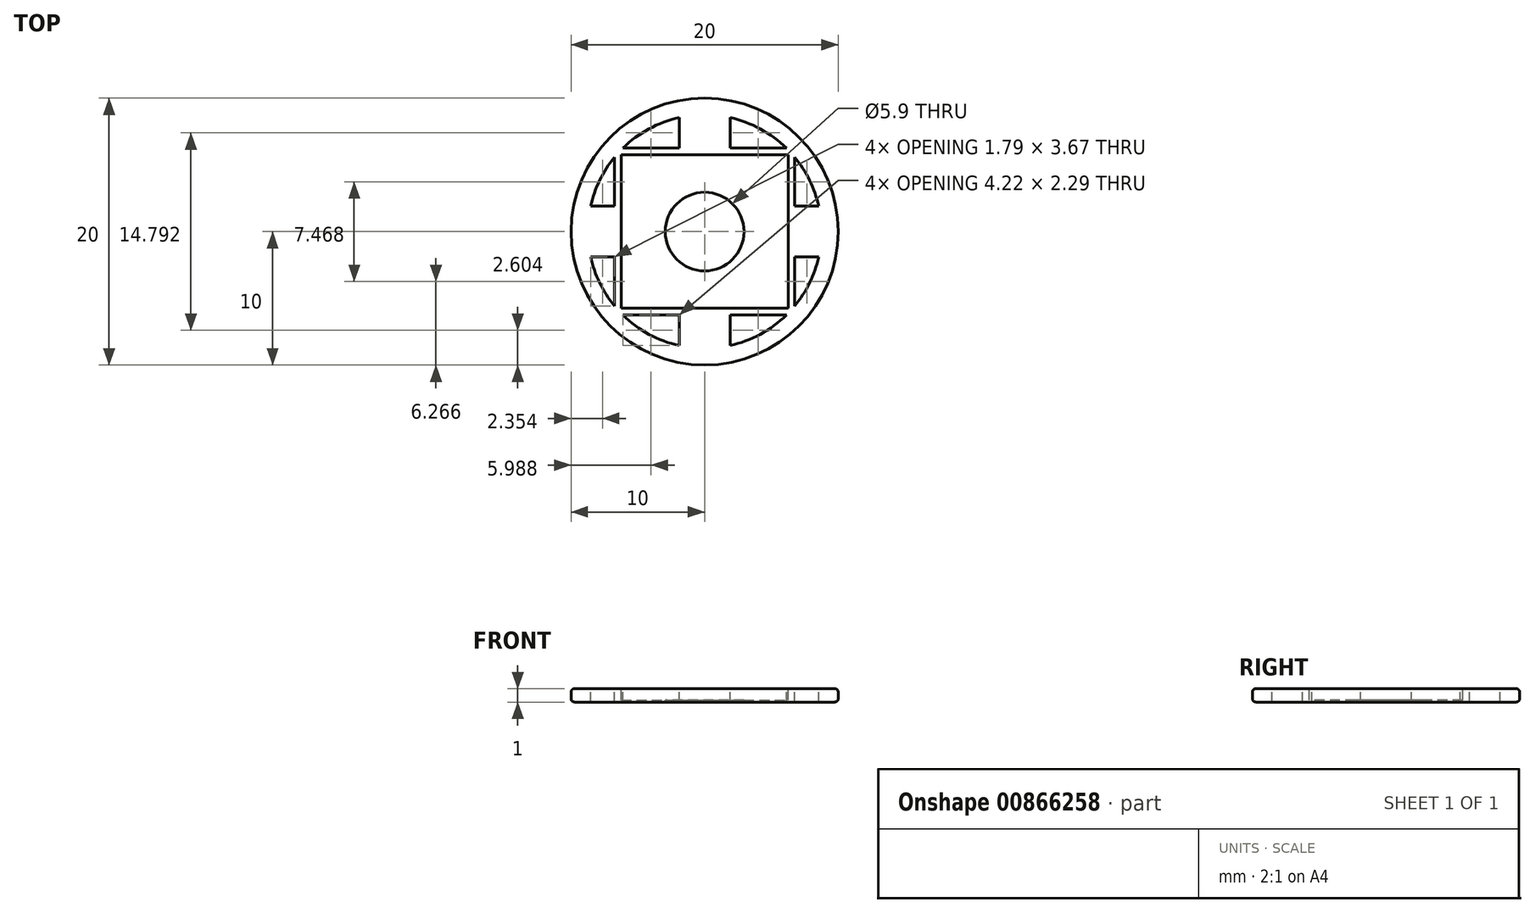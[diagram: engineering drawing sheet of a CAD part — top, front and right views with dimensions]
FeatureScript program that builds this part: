
annotation { "Feature Type Name" : "Feature", "Feature Type Description" : "" }
export const myFeature = defineFeature(function(context is Context, id is Id, definition is map)
    precondition{}
    {
        {
            var Q0;
            Q0=qCreatedBy(makeId("Top.planeOp"),FACE);
            var sketch = newSketch(context, id + "F0", { "sketchPlane" : qUnion([Q0])});
            skCircle(sketch, "E0", {"center": v(0, 0) * mm, "radius": 10 * mm});
            skSolve(sketch);
        }
        {
            var Q0;
            Q0=makeQuery(id+"F0.imprint","IMPRINT",FACE,{"disambiguationData":[TD([[makeQuery(id+"F0.imprint","IMPRINT",EDGE,{"derivedFrom":sQuery(id+"F0.wireOp",EDGE,"E0")}),1.0]])]});
            extrude(context, id + "F1", {"entities" : qUnion([Q0]), "depth" : 1 * mm, "offsetDistance" : 25 * mm});
        }
        {
            var Q0;
            Q0=makeQuery(id+"F1.opExtrude","CAP_FACE",FACE,{"disambiguationData":[OSD([sQuery(id+"F0.wireOp",EDGE,"E0")])],"isStart":false});
            var sketch = newSketch(context, id + "F2", { "sketchPlane" : qUnion([Q0])});
            skLineSegment(sketch, "E1.bottom", {"start": v(-6.25, 5.75) * mm, "end": v(6.25, 5.75) * mm});
            skLineSegment(sketch, "E1.top", {"start": v(-6.25, -5.75) * mm, "end": v(6.25, -5.75) * mm});
            skLineSegment(sketch, "E1.left", {"start": v(-6.25, 5.75) * mm, "end": v(-6.25, -5.75) * mm});
            skLineSegment(sketch, "E1.right", {"start": v(6.25, 5.75) * mm, "end": v(6.25, -5.75) * mm});
            skSolve(sketch);
        }
        {
            var Q0;
            Q0=makeQuery(id+"F2.imprint","IMPRINT",FACE,{"disambiguationData":[TD([[makeQuery(id+"F2.imprint","IMPRINT",EDGE,{"derivedFrom":sQuery(id+"F2.wireOp",EDGE,"E1.bottom")}),-1.0]])]});
            extrude(context, id + "F3", {"entities" : qUnion([Q0]), "operationType" : NewBodyOperationType.REMOVE, "oppositeDirection" : true, "depth" : 0.85 * mm, "offsetDistance" : 25 * mm});
        }
        {
            var Q0;
            Q0=qCreatedBy(makeId("Top.planeOp"),FACE);
            cPlane(context, id + "F4", {"entities" : qUnion([Q0]), "cplaneType" : CPlaneType.OFFSET, "offset" : 0.15 * mm, "width" : 150 * mm, "height" : 150 * mm});
        }
        {
            var Q0;
            Q0=qCreatedBy(id+"F4.planeOp",FACE);
            var sketch = newSketch(context, id + "F5", { "sketchPlane" : qUnion([Q0])});
            skCircle(sketch, "E2", {"center": v(0, 0) * mm, "radius": 2.95 * mm});
            skSolve(sketch);
        }
        {
            var Q0;
            Q0=qSketchRegion(id+"F5",true);
            extrude(context, id + "F6", {"entities" : qUnion([Q0]), "operationType" : NewBodyOperationType.REMOVE, "oppositeDirection" : true, "depth" : 0.15 * mm, "offsetDistance" : 25 * mm});
        }
        {
            var Q0;
            Q0=makeQuery(id+"F1.opExtrude","CAP_EDGE",EDGE,{"disambiguationData":[OSD([sQuery(id+"F0.wireOp",EDGE,"E0")])],"isStart":false});
            var Q1;
            Q1=makeQuery(id+"F1.opExtrude","CAP_EDGE",EDGE,{"disambiguationData":[OSD([sQuery(id+"F0.wireOp",EDGE,"E0")])],"isStart":true});
            var Q2;
            Q2=makeQuery(id+"F1.opExtrude","CAP_EDGE",EDGE,{"disambiguationData":[OSD([sQuery(id+"F0.wireOp",EDGE,"E0")])],"isStart":false});
            fillet(context, id + "F7", {"entities" : qUnion([Q0, Q1, Q2]), "radius" : 0.25 * mm, "tangentPropagation" : true, "allowEdgeOverflow" : false});
        }
        {
            var Q0;
            Q0=makeQuery(id+"F1.opExtrude","CAP_FACE",FACE,{"disambiguationData":[OSD([sQuery(id+"F0.wireOp",EDGE,"E0")])],"isStart":false});
            var sketch = newSketch(context, id + "F8", { "sketchPlane" : qUnion([Q0])});
            skLineSegment(sketch, "E3.bottom", {"start": v(-6.75, 6.25) * mm, "end": v(6.75, 6.25) * mm});
            skLineSegment(sketch, "E3.top", {"start": v(-6.75, -6.25) * mm, "end": v(6.75, -6.25) * mm});
            skLineSegment(sketch, "E3.left", {"start": v(-6.75, 6.25) * mm, "end": v(-6.75, -6.25) * mm});
            skLineSegment(sketch, "E3.right", {"start": v(6.75, 6.25) * mm, "end": v(6.75, -6.25) * mm});
            skPoint(sketch, "E3.middle", {"position": v(0, 0) * mm});
            skCircle(sketch, "E4", {"center": v(0, 0) * mm, "radius": 8.75 * mm});
            skLineSegment(sketch, "E5", {"start": v(-6.75, 1.9) * mm, "end": v(-8.54, 1.9) * mm});
            skLineSegment(sketch, "E6", {"start": v(-1.9, 6.25) * mm, "end": v(-1.9, 8.54) * mm});
            skLineSegment(sketch, "E7", {"start": v(1.9, 6.25) * mm, "end": v(1.9, 8.54) * mm});
            skLineSegment(sketch, "E8", {"start": v(-1.9, -6.25) * mm, "end": v(-1.9, -8.54) * mm});
            skLineSegment(sketch, "E9", {"start": v(1.9, -6.25) * mm, "end": v(1.9, -8.54) * mm});
            skLineSegment(sketch, "E10", {"start": v(-13.45, 0) * mm, "end": v(15.3, 0) * mm, "construction": true});
            skLineSegment(sketch, "E11", {"start": v(0, 11.12) * mm, "end": v(0, -13.32) * mm, "construction": true});
            skLineSegment(sketch, "E12", {"start": v(-6.75, -1.9) * mm, "end": v(-8.54, -1.9) * mm});
            skLineSegment(sketch, "E13", {"start": v(6.75, -1.9) * mm, "end": v(8.54, -1.9) * mm});
            skLineSegment(sketch, "E14", {"start": v(6.75, 1.9) * mm, "end": v(8.54, 1.9) * mm});
            skSolve(sketch);
        }
        {
            var Q0;
            {var subQ0=sQuery(id+"F8.wireOp",EDGE,"REDuOIwV-aCKD-HzUM-NHRB-SqqbAojKLjsp");Q0=makeQuery(id+"F8.imprint","IMPRINT",FACE,{"disambiguationData":[TD([[makeQuery(id+"F8.imprint","IMPRINT",EDGE,{"derivedFrom":subQ0}),1.0]])]});}
            var Q1;
            {var subQ0=sQuery(id+"F8.wireOp",EDGE,"VyAHkpsD-PZa7-2cTz-05Dh-4NWiTEswbYZb");Q1=makeQuery(id+"F8.imprint","IMPRINT",FACE,{"disambiguationData":[TD([[makeQuery(id+"F8.imprint","IMPRINT",EDGE,{"derivedFrom":subQ0}),-1.0]])]});}
            var Q2;
            {var subQ0=sQuery(id+"F8.wireOp",EDGE,"E7");Q2=makeQuery(id+"F8.imprint","IMPRINT",FACE,{"disambiguationData":[TD([[makeQuery(id+"F8.imprint","IMPRINT",EDGE,{"derivedFrom":subQ0}),-1.0]])]});}
            var Q3;
            {var subQ0=sQuery(id+"F8.wireOp",EDGE,"E5");Q3=makeQuery(id+"F8.imprint","IMPRINT",FACE,{"disambiguationData":[TD([[makeQuery(id+"F8.imprint","IMPRINT",EDGE,{"derivedFrom":subQ0}),-1.0]])]});}
            var Q4;
            {var subQ0=sQuery(id+"F8.wireOp",EDGE,"E12");Q4=makeQuery(id+"F8.imprint","IMPRINT",FACE,{"disambiguationData":[TD([[makeQuery(id+"F8.imprint","IMPRINT",EDGE,{"derivedFrom":subQ0}),1.0]])]});}
            var Q5;
            {var subQ0=sQuery(id+"F8.wireOp",EDGE,"E8");Q5=makeQuery(id+"F8.imprint","IMPRINT",FACE,{"disambiguationData":[TD([[makeQuery(id+"F8.imprint","IMPRINT",EDGE,{"derivedFrom":subQ0}),-1.0]])]});}
            var Q6;
            {var subQ0=sQuery(id+"F8.wireOp",EDGE,"E9");Q6=makeQuery(id+"F8.imprint","IMPRINT",FACE,{"disambiguationData":[TD([[makeQuery(id+"F8.imprint","IMPRINT",EDGE,{"derivedFrom":subQ0}),1.0]])]});}
            var Q7;
            {var subQ0=sQuery(id+"F8.wireOp",EDGE,"E13");Q7=makeQuery(id+"F8.imprint","IMPRINT",FACE,{"disambiguationData":[TD([[makeQuery(id+"F8.imprint","IMPRINT",EDGE,{"derivedFrom":subQ0}),-1.0]])]});}
            var Q8;
            {var subQ0=sQuery(id+"F8.wireOp",EDGE,"E14");Q8=makeQuery(id+"F8.imprint","IMPRINT",FACE,{"disambiguationData":[TD([[makeQuery(id+"F8.imprint","IMPRINT",EDGE,{"derivedFrom":subQ0}),1.0]])]});}
            var Q9;
            {var subQ0=sQuery(id+"F8.wireOp",EDGE,"E6");Q9=makeQuery(id+"F8.imprint","IMPRINT",FACE,{"disambiguationData":[TD([[makeQuery(id+"F8.imprint","IMPRINT",EDGE,{"derivedFrom":subQ0}),1.0]])]});}
            extrude(context, id + "F9", {"entities" : qUnion([Q0, Q1, Q2, Q3, Q4, Q5, Q6, Q7, Q8, Q9]), "operationType" : NewBodyOperationType.REMOVE, "endBound" : BoundingType.UP_TO_NEXT, "oppositeDirection" : true, "depth" : 2 * mm, "offsetDistance" : 25 * mm});
        }
    });
